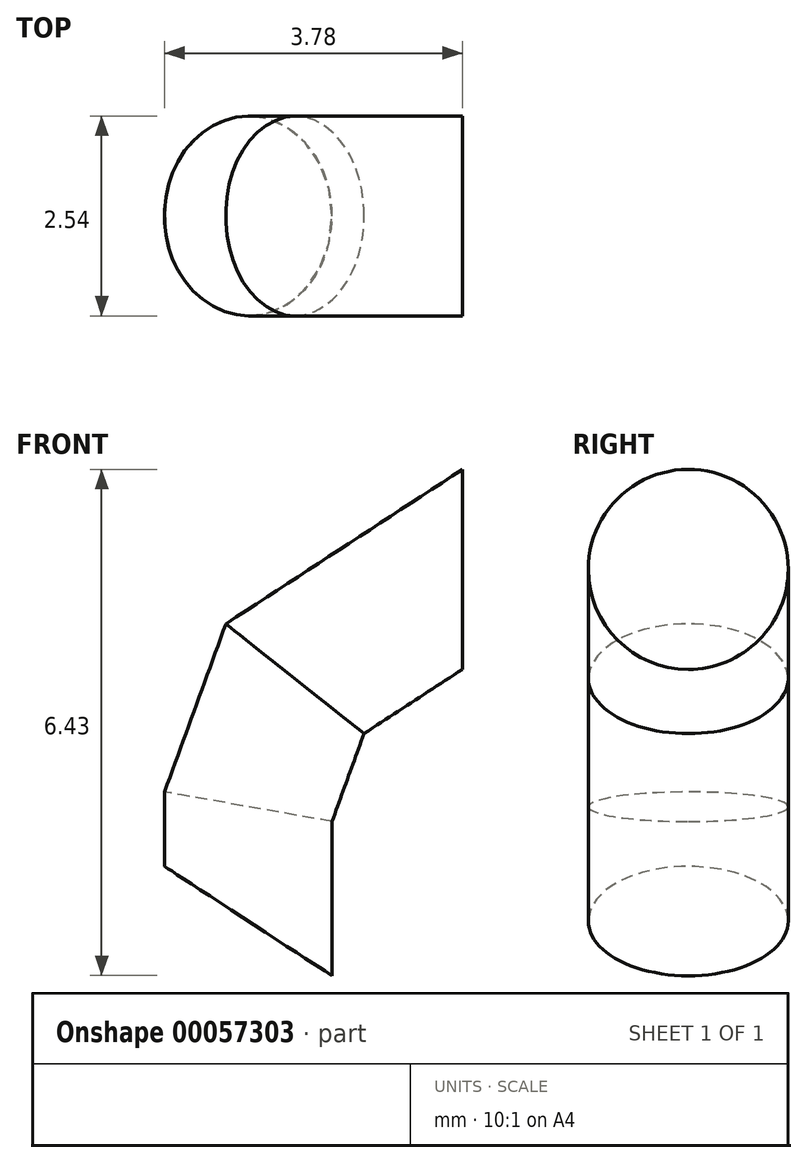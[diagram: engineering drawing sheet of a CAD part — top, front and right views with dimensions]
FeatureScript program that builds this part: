
annotation { "Feature Type Name" : "Feature", "Feature Type Description" : "" }
export const myFeature = defineFeature(function(context is Context, id is Id, definition is map)
    precondition{}
    {
        {
            var Q0;
            Q0=qCreatedBy(makeId("Right.planeOp"),FACE);
            var sketch = newSketch(context, id + "F0", { "sketchPlane" : qUnion([Q0])});
            skCircle(sketch, "E0", {"center": v(0, 0) * mm, "radius": 1.27 * mm});
            skSolve(sketch);
        }
        {
            var Q0;
            Q0=qCreatedBy(makeId("Front.planeOp"),FACE);
            var sketch = newSketch(context, id + "F1", { "sketchPlane" : qUnion([Q0])});
            skLineSegment(sketch, "E1", {"start": v(0, 0) * mm, "end": v(-2.13, -1.39) * mm});
            skLineSegment(sketch, "E2", {"start": v(-2.13, -1.39) * mm, "end": v(-2.72, -3.02) * mm});
            skLineSegment(sketch, "E3", {"start": v(-2.72, -3.02) * mm, "end": v(-2.72, -4.47) * mm});
            skSolve(sketch);
        }
        {
            var Q0;
            Q0=makeQuery(id+"F0.imprint","IMPRINT",FACE,{"disambiguationData":[TD([[makeQuery(id+"F0.imprint","IMPRINT",EDGE,{"derivedFrom":sQuery(id+"F0.wireOp",EDGE,"E0")}),1.0]])]});
            var Q1;
            Q1=sQuery(id+"F1.wireOp",EDGE,"E1");
            var Q2;
            Q2=sQuery(id+"F1.wireOp",EDGE,"E2");
            var Q3;
            Q3=sQuery(id+"F1.wireOp",EDGE,"E3");
            sweep(context, id + "F2", {"profiles" : qUnion([Q0]), "path" : qUnion([Q1, Q2, Q3])});
        }
    });
